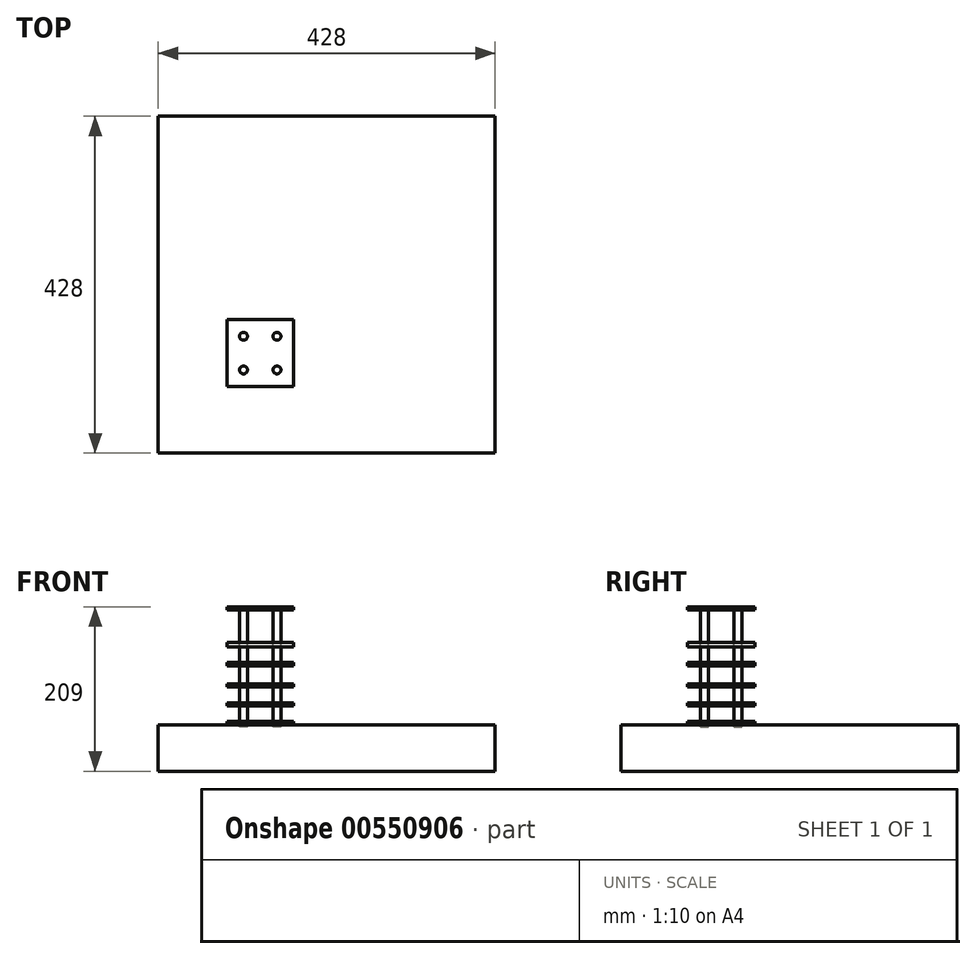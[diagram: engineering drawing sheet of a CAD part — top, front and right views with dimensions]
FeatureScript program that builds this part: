
annotation { "Feature Type Name" : "Feature", "Feature Type Description" : "" }
export const myFeature = defineFeature(function(context is Context, id is Id, definition is map)
    precondition{}
    {
        {
            var Q0;
            Q0=qCreatedBy(makeId("Top.planeOp"),FACE);
            var sketch = newSketch(context, id + "F0", { "sketchPlane" : qUnion([Q0])});
            skLineSegment(sketch, "E0.bottom", {"start": v(214, -214) * mm, "end": v(-214, -214) * mm});
            skLineSegment(sketch, "E0.top", {"start": v(214, 214) * mm, "end": v(-214, 214) * mm});
            skLineSegment(sketch, "E0.left", {"start": v(214, -214) * mm, "end": v(214, 214) * mm});
            skLineSegment(sketch, "E0.right", {"start": v(-214, -214) * mm, "end": v(-214, 214) * mm});
            skPoint(sketch, "E0.middle", {"position": v(0, 0) * mm});
            skSolve(sketch);
        }
        {
            var Q0;
            Q0 = qSketchRegion(id + "F0", true);
            extrude(context, id + "F1", {"entities" : qUnion([Q0]), "depth" : 59 * mm, "offsetDistance" : 25 * mm});
        }
        {
            var Q0;
            Q0=makeQuery(id+"F1.opExtrude","CAP_FACE",FACE,{"disambiguationData":[OSD([sQuery(id+"F0.wireOp",EDGE,"E0.bottom"),sQuery(id+"F0.wireOp",EDGE,"E0.top"),sQuery(id+"F0.wireOp",EDGE,"E0.left"),sQuery(id+"F0.wireOp",EDGE,"E0.right")])],"isStart":false});
            var sketch = newSketch(context, id + "F2", { "sketchPlane" : qUnion([Q0])});
            skLineSegment(sketch, "E1.bottom", {"start": v(-214, 214) * mm, "end": v(-39, 214) * mm});
            skLineSegment(sketch, "E1.top", {"start": v(-214, 39) * mm, "end": v(-39, 39) * mm});
            skLineSegment(sketch, "E1.left", {"start": v(-214, 214) * mm, "end": v(-214, 39) * mm});
            skLineSegment(sketch, "E1.right", {"start": v(-39, 214) * mm, "end": v(-39, 39) * mm});
            skLineSegment(sketch, "E2.bottom", {"start": v(214, -214) * mm, "end": v(39, -214) * mm});
            skLineSegment(sketch, "E2.top", {"start": v(214, -39) * mm, "end": v(39, -39) * mm});
            skLineSegment(sketch, "E2.left", {"start": v(214, -214) * mm, "end": v(214, -39) * mm});
            skLineSegment(sketch, "E2.right", {"start": v(39, -214) * mm, "end": v(39, -39) * mm});
            skLineSegment(sketch, "E3.bottom", {"start": v(43.05, 128.67) * mm, "end": v(128.44, 128.67) * mm, "construction": true});
            skLineSegment(sketch, "E3.top", {"start": v(43.05, 42.87) * mm, "end": v(128.44, 42.87) * mm, "construction": true});
            skLineSegment(sketch, "E3.left", {"start": v(43.05, 128.67) * mm, "end": v(43.05, 42.87) * mm, "construction": true});
            skLineSegment(sketch, "E3.right", {"start": v(128.44, 128.67) * mm, "end": v(128.44, 42.87) * mm, "construction": true});
            skLineSegment(sketch, "E4.bottom", {"start": v(-126.92, -44.16) * mm, "end": v(-41.94, -44.16) * mm, "construction": true});
            skLineSegment(sketch, "E4.top", {"start": v(-126.92, -129.56) * mm, "end": v(-41.94, -129.56) * mm, "construction": true});
            skLineSegment(sketch, "E4.left", {"start": v(-126.92, -44.16) * mm, "end": v(-126.92, -129.56) * mm, "construction": true});
            skLineSegment(sketch, "E4.right", {"start": v(-41.94, -44.16) * mm, "end": v(-41.94, -129.56) * mm, "construction": true});
            skLineSegment(sketch, "E5.bottom", {"start": v(-41.94, -129.56) * mm, "end": v(-126.92, -129.56) * mm, "construction": true});
            skLineSegment(sketch, "E5.top", {"start": v(-41.94, -86.86) * mm, "end": v(-126.92, -86.86) * mm, "construction": true});
            skLineSegment(sketch, "E5.left", {"start": v(-41.94, -129.56) * mm, "end": v(-41.94, -86.86) * mm, "construction": true});
            skLineSegment(sketch, "E5.right", {"start": v(-126.92, -129.56) * mm, "end": v(-126.92, -86.86) * mm, "construction": true});
            skLineSegment(sketch, "E6.bottom", {"start": v(-126.92, -86.86) * mm, "end": v(-84.43, -86.86) * mm, "construction": true});
            skLineSegment(sketch, "E6.top", {"start": v(-126.92, -129.56) * mm, "end": v(-84.43, -129.56) * mm, "construction": true});
            skLineSegment(sketch, "E6.left", {"start": v(-126.92, -86.86) * mm, "end": v(-126.92, -129.56) * mm, "construction": true});
            skLineSegment(sketch, "E6.right", {"start": v(-84.43, -86.86) * mm, "end": v(-84.43, -129.56) * mm, "construction": true});
            skLineSegment(sketch, "E7.top", {"start": v(43.05, 85.77) * mm, "end": v(128.44, 85.77) * mm, "construction": true});
            skLineSegment(sketch, "E7.left", {"start": v(43.05, 42.87) * mm, "end": v(43.05, 85.77) * mm, "construction": true});
            skLineSegment(sketch, "E7.right", {"start": v(128.44, 42.87) * mm, "end": v(128.44, 85.77) * mm, "construction": true});
            skLineSegment(sketch, "E8.bottom", {"start": v(128.44, 85.77) * mm, "end": v(85.75, 85.77) * mm, "construction": true});
            skLineSegment(sketch, "E8.top", {"start": v(128.44, 42.87) * mm, "end": v(85.75, 42.87) * mm, "construction": true});
            skLineSegment(sketch, "E8.left", {"start": v(128.44, 85.77) * mm, "end": v(128.44, 42.87) * mm, "construction": true});
            skLineSegment(sketch, "E8.right", {"start": v(85.75, 85.77) * mm, "end": v(85.75, 42.87) * mm, "construction": true});
            skLineSegment(sketch, "E9.bottom", {"start": v(43.05, 128.67) * mm, "end": v(128.44, 128.67) * mm});
            skLineSegment(sketch, "E9.top", {"start": v(43.05, 42.87) * mm, "end": v(128.44, 42.87) * mm});
            skLineSegment(sketch, "E9.left", {"start": v(43.05, 128.67) * mm, "end": v(43.05, 42.87) * mm});
            skLineSegment(sketch, "E9.right", {"start": v(128.44, 128.67) * mm, "end": v(128.44, 42.87) * mm});
            skPoint(sketch, "E9.middle", {"position": v(85.75, 85.77) * mm});
            skLineSegment(sketch, "E10.bottom", {"start": v(-126.92, -44.16) * mm, "end": v(-41.94, -44.16) * mm});
            skLineSegment(sketch, "E10.top", {"start": v(-126.92, -129.56) * mm, "end": v(-41.94, -129.56) * mm});
            skLineSegment(sketch, "E10.left", {"start": v(-126.92, -44.16) * mm, "end": v(-126.92, -129.56) * mm});
            skLineSegment(sketch, "E10.right", {"start": v(-41.94, -44.16) * mm, "end": v(-41.94, -129.56) * mm});
            skPoint(sketch, "E10.middle", {"position": v(-84.43, -86.86) * mm});
            skLineSegment(sketch, "E11.bottom", {"start": v(-39, 39) * mm, "end": v(-214, 39) * mm});
            skLineSegment(sketch, "E11.top", {"start": v(-39, 126.5) * mm, "end": v(-214, 126.5) * mm});
            skLineSegment(sketch, "E11.left", {"start": v(-39, 39) * mm, "end": v(-39, 126.5) * mm});
            skLineSegment(sketch, "E11.right", {"start": v(-214, 39) * mm, "end": v(-214, 126.5) * mm});
            skLineSegment(sketch, "E12.bottom", {"start": v(-39, 126.5) * mm, "end": v(-126.5, 126.5) * mm});
            skLineSegment(sketch, "E12.top", {"start": v(-39, 214) * mm, "end": v(-126.5, 214) * mm});
            skLineSegment(sketch, "E12.left", {"start": v(-39, 126.5) * mm, "end": v(-39, 214) * mm});
            skLineSegment(sketch, "E12.right", {"start": v(-126.5, 126.5) * mm, "end": v(-126.5, 214) * mm});
            skLineSegment(sketch, "E13.top", {"start": v(214, -126.5) * mm, "end": v(39, -126.5) * mm});
            skLineSegment(sketch, "E13.left", {"start": v(214, -39) * mm, "end": v(214, -126.5) * mm});
            skLineSegment(sketch, "E13.right", {"start": v(39, -39) * mm, "end": v(39, -126.5) * mm});
            skLineSegment(sketch, "E14.bottom", {"start": v(39, -126.5) * mm, "end": v(126.5, -126.5) * mm});
            skLineSegment(sketch, "E14.top", {"start": v(39, -214) * mm, "end": v(126.5, -214) * mm});
            skLineSegment(sketch, "E14.left", {"start": v(39, -126.5) * mm, "end": v(39, -214) * mm});
            skLineSegment(sketch, "E14.right", {"start": v(126.5, -126.5) * mm, "end": v(126.5, -214) * mm});
            skSolve(sketch);
        }
        {
            var Q0;
            Q0=makeQuery(id+"F2.imprint","IMPRINT",FACE,{"disambiguationData":[TD([[makeQuery(id+"F2.imprint","IMPRINT",EDGE,{"derivedFrom":sQuery(id+"F2.wireOp",EDGE,"E10.bottom")}),-1.0]])]});
            extrude(context, id + "F3", {"entities" : qUnion([Q0]), "operationType" : NewBodyOperationType.ADD, "depth" : 150 * mm, "offsetDistance" : 25 * mm});
        }
        {
            var Q0;
            Q0=makeQuery(id+"F3.opExtrude","CAP_FACE",FACE,{"disambiguationData":[OSD([sQuery(id+"F2.wireOp",EDGE,"E10.bottom"),sQuery(id+"F2.wireOp",EDGE,"E10.top"),sQuery(id+"F2.wireOp",EDGE,"E10.left"),sQuery(id+"F2.wireOp",EDGE,"E10.right")])],"isStart":false});
            var sketch = newSketch(context, id + "F4", { "sketchPlane" : qUnion([Q0])});
            skLineSegment(sketch, "E15.bottom", {"start": v(-126.92, -44.16) * mm, "end": v(-41.94, -44.16) * mm, "construction": true});
            skLineSegment(sketch, "E15.top", {"start": v(-126.92, -129.56) * mm, "end": v(-41.94, -129.56) * mm, "construction": true});
            skLineSegment(sketch, "E15.left", {"start": v(-126.92, -44.16) * mm, "end": v(-126.92, -129.56) * mm, "construction": true});
            skLineSegment(sketch, "E15.right", {"start": v(-41.94, -44.16) * mm, "end": v(-41.94, -129.56) * mm, "construction": true});
            skLineSegment(sketch, "E16.bottom", {"start": v(-41.94, -129.56) * mm, "end": v(-84.43, -129.56) * mm, "construction": true});
            skLineSegment(sketch, "E16.top", {"start": v(-41.94, -44.16) * mm, "end": v(-84.43, -44.16) * mm, "construction": true});
            skLineSegment(sketch, "E16.left", {"start": v(-41.94, -129.56) * mm, "end": v(-41.94, -44.16) * mm, "construction": true});
            skLineSegment(sketch, "E16.right", {"start": v(-84.43, -129.56) * mm, "end": v(-84.43, -44.16) * mm, "construction": true});
            skLineSegment(sketch, "E17.top", {"start": v(-126.92, -86.86) * mm, "end": v(-41.94, -86.86) * mm, "construction": true});
            skLineSegment(sketch, "E17.left", {"start": v(-126.92, -44.16) * mm, "end": v(-126.92, -86.86) * mm, "construction": true});
            skLineSegment(sketch, "E17.right", {"start": v(-41.94, -44.16) * mm, "end": v(-41.94, -86.86) * mm, "construction": true});
            skLineSegment(sketch, "E18.top", {"start": v(-126.92, -65.51) * mm, "end": v(-41.94, -65.51) * mm, "construction": true});
            skLineSegment(sketch, "E18.left", {"start": v(-126.92, -44.16) * mm, "end": v(-126.92, -65.51) * mm, "construction": true});
            skLineSegment(sketch, "E18.right", {"start": v(-41.94, -44.16) * mm, "end": v(-41.94, -65.51) * mm, "construction": true});
            skLineSegment(sketch, "E19.top", {"start": v(-41.94, -86.86) * mm, "end": v(-84.43, -86.86) * mm, "construction": true});
            skLineSegment(sketch, "E19.left", {"start": v(-41.94, -129.56) * mm, "end": v(-41.94, -86.86) * mm, "construction": true});
            skLineSegment(sketch, "E19.right", {"start": v(-84.43, -129.56) * mm, "end": v(-84.43, -86.86) * mm, "construction": true});
            skLineSegment(sketch, "E20.top", {"start": v(-41.94, -108.2) * mm, "end": v(-84.43, -108.2) * mm, "construction": true});
            skLineSegment(sketch, "E20.left", {"start": v(-41.94, -129.56) * mm, "end": v(-41.94, -108.2) * mm, "construction": true});
            skLineSegment(sketch, "E20.right", {"start": v(-84.43, -129.56) * mm, "end": v(-84.43, -108.2) * mm, "construction": true});
            skLineSegment(sketch, "E21.bottom", {"start": v(-126.92, -86.86) * mm, "end": v(-63.18, -86.86) * mm, "construction": true});
            skLineSegment(sketch, "E21.top", {"start": v(-126.92, -129.56) * mm, "end": v(-63.18, -129.56) * mm, "construction": true});
            skLineSegment(sketch, "E21.left", {"start": v(-126.92, -86.86) * mm, "end": v(-126.92, -129.56) * mm, "construction": true});
            skLineSegment(sketch, "E21.right", {"start": v(-63.18, -86.86) * mm, "end": v(-63.18, -129.56) * mm, "construction": true});
            skLineSegment(sketch, "E22.bottom", {"start": v(-41.94, -129.56) * mm, "end": v(-126.92, -129.56) * mm, "construction": true});
            skLineSegment(sketch, "E22.top", {"start": v(-41.94, -108.2) * mm, "end": v(-126.92, -108.2) * mm, "construction": true});
            skLineSegment(sketch, "E22.right", {"start": v(-126.92, -129.56) * mm, "end": v(-126.92, -108.2) * mm, "construction": true});
            skLineSegment(sketch, "E23.bottom", {"start": v(-126.92, -44.16) * mm, "end": v(-84.43, -44.16) * mm, "construction": true});
            skLineSegment(sketch, "E23.top", {"start": v(-126.92, -129.56) * mm, "end": v(-84.43, -129.56) * mm, "construction": true});
            skLineSegment(sketch, "E23.right", {"start": v(-84.43, -44.16) * mm, "end": v(-84.43, -129.56) * mm, "construction": true});
            skLineSegment(sketch, "E24.bottom", {"start": v(-84.43, -129.56) * mm, "end": v(-105.68, -129.56) * mm, "construction": true});
            skLineSegment(sketch, "E24.top", {"start": v(-84.43, -44.16) * mm, "end": v(-105.68, -44.16) * mm, "construction": true});
            skLineSegment(sketch, "E24.right", {"start": v(-105.68, -129.56) * mm, "end": v(-105.68, -44.16) * mm, "construction": true});
            skLineSegment(sketch, "E25.bottom", {"start": v(-84.43, -44.16) * mm, "end": v(-63.18, -44.16) * mm, "construction": true});
            skLineSegment(sketch, "E25.top", {"start": v(-84.43, -129.56) * mm, "end": v(-63.18, -129.56) * mm, "construction": true});
            skLineSegment(sketch, "E25.right", {"start": v(-63.18, -44.16) * mm, "end": v(-63.18, -129.56) * mm, "construction": true});
            skCircle(sketch, "E26", {"center": v(-105.68, -65.51) * mm, "radius": 5 * mm});
            skCircle(sketch, "E27", {"center": v(-105.68, -108.2) * mm, "radius": 5 * mm});
            skCircle(sketch, "E28", {"center": v(-63.18, -108.2) * mm, "radius": 5 * mm});
            skCircle(sketch, "E29", {"center": v(-63.18, -65.51) * mm, "radius": 5 * mm});
            skSolve(sketch);
        }
        {
            var Q0;
            Q0=makeQuery(id+"F3.opExtrude","SWEPT_FACE",FACE,{"disambiguationData":[OSD([sQuery(id+"F2.wireOp",EDGE,"E10.top")])]});
            var sketch = newSketch(context, id + "F5", { "sketchPlane" : qUnion([Q0])});
            skLineSegment(sketch, "E30.bottom", {"start": v(-126.92, 209) * mm, "end": v(-41.94, 209) * mm, "construction": true});
            skLineSegment(sketch, "E30.top", {"start": v(-126.92, 205) * mm, "end": v(-41.94, 205) * mm, "construction": true});
            skLineSegment(sketch, "E30.left", {"start": v(-126.92, 209) * mm, "end": v(-126.92, 205) * mm, "construction": true});
            skLineSegment(sketch, "E30.right", {"start": v(-41.94, 209) * mm, "end": v(-41.94, 205) * mm, "construction": true});
            skLineSegment(sketch, "E31.bottom", {"start": v(-126.92, 59) * mm, "end": v(-41.94, 59) * mm, "construction": true});
            skLineSegment(sketch, "E31.top", {"start": v(-126.92, 63) * mm, "end": v(-41.94, 63) * mm, "construction": true});
            skLineSegment(sketch, "E31.left", {"start": v(-126.92, 59) * mm, "end": v(-126.92, 63) * mm, "construction": true});
            skLineSegment(sketch, "E31.right", {"start": v(-41.94, 59) * mm, "end": v(-41.94, 63) * mm, "construction": true});
            skLineSegment(sketch, "E32.bottom", {"start": v(-126.92, 63) * mm, "end": v(-41.94, 63) * mm});
            skLineSegment(sketch, "E32.top", {"start": v(-126.92, 83) * mm, "end": v(-41.94, 83) * mm});
            skLineSegment(sketch, "E32.left", {"start": v(-126.92, 63) * mm, "end": v(-126.92, 83) * mm});
            skLineSegment(sketch, "E32.right", {"start": v(-41.94, 63) * mm, "end": v(-41.94, 83) * mm});
            skLineSegment(sketch, "E33.bottom", {"start": v(-126.92, 83) * mm, "end": v(-41.94, 83) * mm, "construction": true});
            skLineSegment(sketch, "E33.top", {"start": v(-126.92, 87) * mm, "end": v(-41.94, 87) * mm, "construction": true});
            skLineSegment(sketch, "E33.left", {"start": v(-126.92, 83) * mm, "end": v(-126.92, 87) * mm, "construction": true});
            skLineSegment(sketch, "E33.right", {"start": v(-41.94, 83) * mm, "end": v(-41.94, 87) * mm, "construction": true});
            skLineSegment(sketch, "E34.bottom", {"start": v(-126.92, 87) * mm, "end": v(-41.94, 87) * mm});
            skLineSegment(sketch, "E34.top", {"start": v(-126.92, 107) * mm, "end": v(-41.94, 107) * mm});
            skLineSegment(sketch, "E34.left", {"start": v(-126.92, 87) * mm, "end": v(-126.92, 107) * mm});
            skLineSegment(sketch, "E34.right", {"start": v(-41.94, 87) * mm, "end": v(-41.94, 107) * mm});
            skLineSegment(sketch, "E35.bottom", {"start": v(-126.92, 107) * mm, "end": v(-41.94, 107) * mm, "construction": true});
            skLineSegment(sketch, "E35.top", {"start": v(-126.92, 111) * mm, "end": v(-41.94, 111) * mm, "construction": true});
            skLineSegment(sketch, "E35.left", {"start": v(-126.92, 107) * mm, "end": v(-126.92, 111) * mm, "construction": true});
            skLineSegment(sketch, "E35.right", {"start": v(-41.94, 107) * mm, "end": v(-41.94, 111) * mm, "construction": true});
            skLineSegment(sketch, "E36.bottom", {"start": v(-126.92, 111) * mm, "end": v(-41.94, 111) * mm});
            skLineSegment(sketch, "E36.top", {"start": v(-126.92, 134) * mm, "end": v(-41.94, 134) * mm});
            skLineSegment(sketch, "E36.left", {"start": v(-126.92, 111) * mm, "end": v(-126.92, 134) * mm});
            skLineSegment(sketch, "E36.right", {"start": v(-41.94, 111) * mm, "end": v(-41.94, 134) * mm});
            skLineSegment(sketch, "E37.bottom", {"start": v(-126.92, 134) * mm, "end": v(-41.94, 134) * mm, "construction": true});
            skLineSegment(sketch, "E37.top", {"start": v(-126.92, 138) * mm, "end": v(-41.94, 138) * mm, "construction": true});
            skLineSegment(sketch, "E37.left", {"start": v(-126.92, 134) * mm, "end": v(-126.92, 138) * mm, "construction": true});
            skLineSegment(sketch, "E37.right", {"start": v(-41.94, 134) * mm, "end": v(-41.94, 138) * mm, "construction": true});
            skLineSegment(sketch, "E38.bottom", {"start": v(-126.92, 138) * mm, "end": v(-41.94, 138) * mm});
            skLineSegment(sketch, "E38.top", {"start": v(-126.92, 158) * mm, "end": v(-41.94, 158) * mm});
            skLineSegment(sketch, "E38.left", {"start": v(-126.92, 138) * mm, "end": v(-126.92, 158) * mm});
            skLineSegment(sketch, "E38.right", {"start": v(-41.94, 138) * mm, "end": v(-41.94, 158) * mm});
            skLineSegment(sketch, "E39.bottom", {"start": v(-126.92, 158) * mm, "end": v(-41.94, 158) * mm, "construction": true});
            skLineSegment(sketch, "E39.top", {"start": v(-126.92, 163.52) * mm, "end": v(-41.94, 163.52) * mm, "construction": true});
            skLineSegment(sketch, "E39.left", {"start": v(-126.92, 158) * mm, "end": v(-126.92, 163.52) * mm, "construction": true});
            skLineSegment(sketch, "E39.right", {"start": v(-41.94, 158) * mm, "end": v(-41.94, 163.52) * mm, "construction": true});
            skLineSegment(sketch, "E40.bottom", {"start": v(-126.92, 163.52) * mm, "end": v(-124.78, 163.52) * mm});
            skLineSegment(sketch, "E40.top", {"start": v(-126.92, 163.52) * mm, "end": v(-124.78, 163.52) * mm});
            skLineSegment(sketch, "E40.left", {"start": v(-126.92, 163.52) * mm, "end": v(-126.92, 163.52) * mm});
            skLineSegment(sketch, "E40.right", {"start": v(-124.78, 163.52) * mm, "end": v(-124.78, 163.52) * mm});
            skLineSegment(sketch, "E41.bottom", {"start": v(-41.94, 205) * mm, "end": v(-126.92, 205) * mm});
            skLineSegment(sketch, "E41.top", {"start": v(-41.94, 163.52) * mm, "end": v(-126.92, 163.52) * mm});
            skLineSegment(sketch, "E41.left", {"start": v(-41.94, 205) * mm, "end": v(-41.94, 163.52) * mm});
            skLineSegment(sketch, "E41.right", {"start": v(-126.92, 205) * mm, "end": v(-126.92, 163.52) * mm});
            skSolve(sketch);
        }
        {
            var Q0;
            Q0 = qSketchRegion(id + "F5", true);
            extrude(context, id + "F6", {"entities" : qUnion([Q0]), "operationType" : NewBodyOperationType.REMOVE, "oppositeDirection" : true, "depth" : 100 * mm, "offsetDistance" : 25 * mm});
        }
        {
            var Q0;
            Q0 = qSketchRegion(id + "F4", true);
            extrude(context, id + "F7", {"entities" : qUnion([Q0]), "oppositeDirection" : true, "depth" : 153 * mm, "offsetDistance" : 25 * mm});
        }
    });
